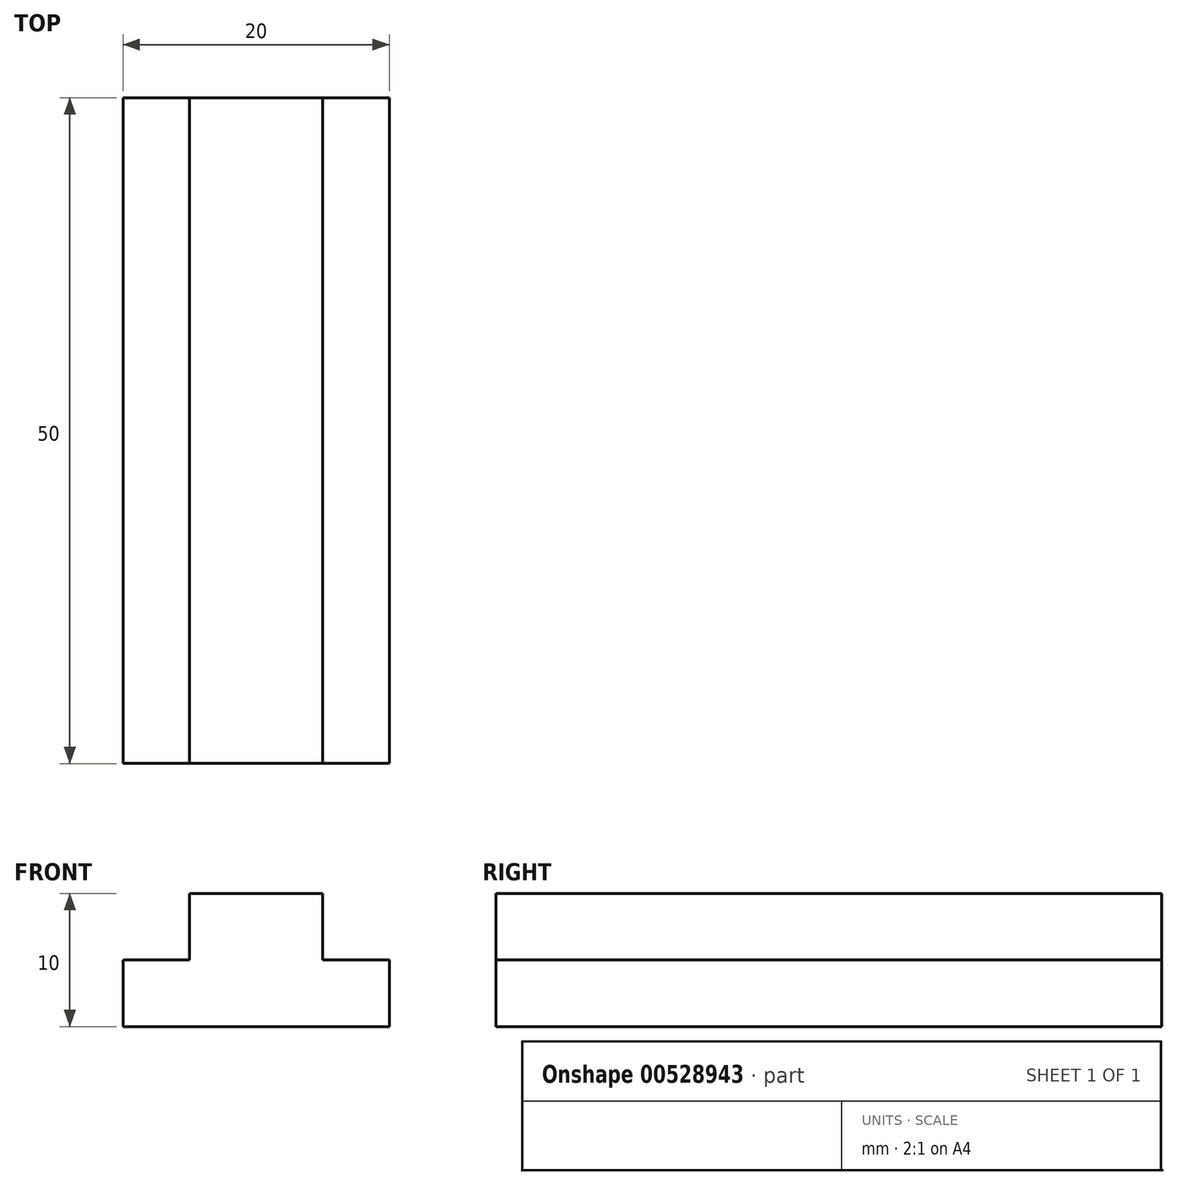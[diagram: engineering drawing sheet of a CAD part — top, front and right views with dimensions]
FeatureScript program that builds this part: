
annotation { "Feature Type Name" : "Feature", "Feature Type Description" : "" }
export const myFeature = defineFeature(function(context is Context, id is Id, definition is map)
    precondition{}
    {
        {
            var Q0;
            Q0=qCreatedBy(makeId("Top.planeOp"),FACE);
            var sketch = newSketch(context, id + "F0", { "sketchPlane" : qUnion([Q0])});
            skLineSegment(sketch, "E0.bottom", {"start": v(-36.16, 14.3) * mm, "end": v(-46.16, 14.3) * mm});
            skLineSegment(sketch, "E0.top", {"start": v(-36.16, 64.3) * mm, "end": v(-46.16, 64.3) * mm});
            skLineSegment(sketch, "E0.left", {"start": v(-36.16, 14.3) * mm, "end": v(-36.16, 64.3) * mm});
            skLineSegment(sketch, "E0.right", {"start": v(-46.16, 14.3) * mm, "end": v(-46.16, 64.3) * mm});
            skPoint(sketch, "E0.middle", {"position": v(-41.16, 39.3) * mm});
            skSolve(sketch);
        }
        {
            var Q0;
            Q0=makeQuery(id+"F0.imprint","IMPRINT",FACE,{"disambiguationData":[TD([[makeQuery(id+"F0.imprint","IMPRINT",EDGE,{"derivedFrom":sQuery(id+"F0.wireOp",EDGE,"E0.bottom")}),-1.0]])]});
            extrude(context, id + "F1", {"entities" : qUnion([Q0]), "depth" : 10 * mm, "offsetDistance" : 25 * mm});
        }
        {
            var Q0;
            Q0=makeQuery(id+"F1.opExtrude","SWEPT_FACE",FACE,{"disambiguationData":[OSD([sQuery(id+"F0.wireOp",EDGE,"E0.left")])]});
            var sketch = newSketch(context, id + "F2", { "sketchPlane" : qUnion([Q0])});
            skLineSegment(sketch, "E1.bottom", {"start": v(14.3, 0) * mm, "end": v(64.3, 0) * mm});
            skLineSegment(sketch, "E1.top", {"start": v(14.3, 5) * mm, "end": v(64.3, 5) * mm});
            skLineSegment(sketch, "E1.left", {"start": v(14.3, 0) * mm, "end": v(14.3, 5) * mm});
            skLineSegment(sketch, "E1.right", {"start": v(64.3, 0) * mm, "end": v(64.3, 5) * mm});
            skSolve(sketch);
        }
        {
            var Q0;
            Q0=makeQuery(id+"F2.imprint","IMPRINT",FACE,{"disambiguationData":[TD([[makeQuery(id+"F2.imprint","IMPRINT",EDGE,{"derivedFrom":sQuery(id+"F2.wireOp",EDGE,"E1.bottom")}),1.0]])]});
            extrude(context, id + "F3", {"entities" : qUnion([Q0]), "operationType" : NewBodyOperationType.ADD, "depth" : 5 * mm, "offsetDistance" : 25 * mm});
        }
        {
            var Q0;
            Q0=makeQuery(id+"F1.opExtrude","SWEPT_FACE",FACE,{"disambiguationData":[OSD([sQuery(id+"F0.wireOp",EDGE,"E0.right")])]});
            var sketch = newSketch(context, id + "F4", { "sketchPlane" : qUnion([Q0])});
            skLineSegment(sketch, "E2.bottom", {"start": v(-64.3, 0) * mm, "end": v(-14.3, 0) * mm});
            skLineSegment(sketch, "E2.top", {"start": v(-64.3, 5) * mm, "end": v(-14.3, 5) * mm});
            skLineSegment(sketch, "E2.left", {"start": v(-64.3, 0) * mm, "end": v(-64.3, 5) * mm});
            skLineSegment(sketch, "E2.right", {"start": v(-14.3, 0) * mm, "end": v(-14.3, 5) * mm});
            skSolve(sketch);
        }
        {
            var Q0;
            Q0=makeQuery(id+"F4.imprint","IMPRINT",FACE,{"disambiguationData":[TD([[makeQuery(id+"F4.imprint","IMPRINT",EDGE,{"derivedFrom":sQuery(id+"F4.wireOp",EDGE,"E2.bottom")}),-1.0]])]});
            extrude(context, id + "F5", {"entities" : qUnion([Q0]), "operationType" : NewBodyOperationType.ADD, "depth" : 5 * mm, "offsetDistance" : 25 * mm});
        }
    });
